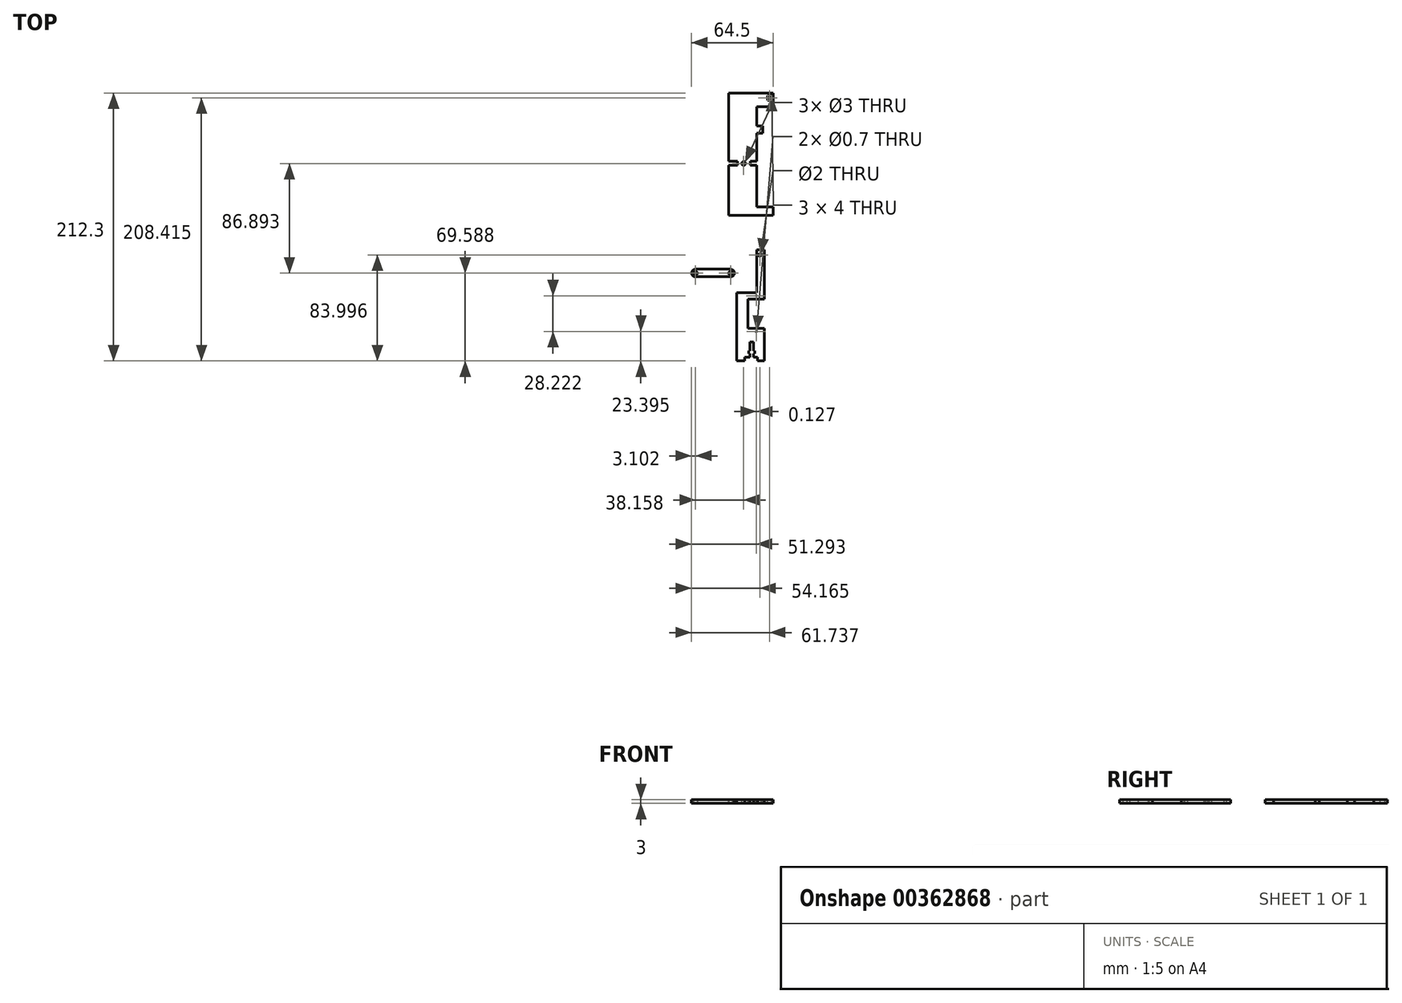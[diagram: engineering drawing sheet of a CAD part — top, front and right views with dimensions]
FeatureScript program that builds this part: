
annotation { "Feature Type Name" : "Feature", "Feature Type Description" : "" }
export const myFeature = defineFeature(function(context is Context, id is Id, definition is map)
    precondition{}
    {
        {
            var Q0;
            Q0=qCreatedBy(makeId("Top.planeOp"),FACE);
            var sketch = newSketch(context, id + "F0", { "sketchPlane" : qUnion([Q0])});
            skLineSegment(sketch, "E0.bottom", {"start": v(-45.73, -4.7) * mm, "end": v(-11.73, -4.7) * mm});
            skLineSegment(sketch, "E0.top", {"start": v(-45.73, 1.3) * mm, "end": v(-11.73, 1.3) * mm});
            skLineSegment(sketch, "E0.left", {"start": v(-45.73, -4.7) * mm, "end": v(-45.73, 1.3) * mm});
            skLineSegment(sketch, "E0.right", {"start": v(-11.73, -4.7) * mm, "end": v(-11.73, 1.3) * mm});
            skSolve(sketch);
        }
        {
            var Q0;
            Q0 = qSketchRegion(id + "F0", true);
            extrude(context, id + "F1", {"entities" : qUnion([Q0]), "depth" : 3 * mm});
        }
        {
            var Q0;
            Q0=makeQuery(id+"F1.opExtrude","SWEPT_EDGE",EDGE,{"disambiguationData":[OSD([sQuery(id+"F0.wireOp",EDGE,"E0.bottom"),sQuery(id+"F0.wireOp",EDGE,"E0.right")])]});
            var Q1;
            Q1=makeQuery(id+"F1.opExtrude","SWEPT_EDGE",EDGE,{"disambiguationData":[OSD([sQuery(id+"F0.wireOp",EDGE,"E0.top"),sQuery(id+"F0.wireOp",EDGE,"E0.right")])]});
            fillet(context, id + "F2", {"entities" : qUnion([Q0, Q1]), "radius" : 3.1 * mm, "tangentPropagation" : true, "allowEdgeOverflow" : false});
        }
        {
            var Q0;
            Q0=makeQuery(id+"F1.opExtrude","SWEPT_EDGE",EDGE,{"disambiguationData":[OSD([sQuery(id+"F0.wireOp",EDGE,"E0.bottom"),sQuery(id+"F0.wireOp",EDGE,"E0.left")])]});
            var Q1;
            Q1=makeQuery(id+"F1.opExtrude","SWEPT_EDGE",EDGE,{"disambiguationData":[OSD([sQuery(id+"F0.wireOp",EDGE,"E0.top"),sQuery(id+"F0.wireOp",EDGE,"E0.left")])]});
            fillet(context, id + "F3", {"entities" : qUnion([Q0, Q1]), "radius" : 3.1 * mm, "tangentPropagation" : true, "allowEdgeOverflow" : false});
        }
        {
            var Q0;
            Q0=makeQuery(id+"F1.opExtrude","CAP_FACE",FACE,{"disambiguationData":[OSD([sQuery(id+"F0.wireOp",EDGE,"E0.bottom"),sQuery(id+"F0.wireOp",EDGE,"E0.top"),sQuery(id+"F0.wireOp",EDGE,"E0.left"),sQuery(id+"F0.wireOp",EDGE,"E0.right")])],"isStart":true});
            var sketch = newSketch(context, id + "F4", { "sketchPlane" : qUnion([Q0])});
            skCircle(sketch, "E1", {"center": v(-42.63, 1.8) * mm, "radius": 1.5 * mm});
            skCircle(sketch, "E2", {"center": v(-14.83, 1.8) * mm, "radius": 1.5 * mm});
            skSolve(sketch);
        }
        {
            var Q0;
            Q0 = qSketchRegion(id + "F4", true);
            extrude(context, id + "F5", {"entities" : qUnion([Q0]), "operationType" : NewBodyOperationType.REMOVE, "oppositeDirection" : true, "depth" : 25.8 * mm});
        }
        {
            var Q0;
            Q0=qCreatedBy(makeId("Top.planeOp"),FACE);
            var sketch = newSketch(context, id + "F6", { "sketchPlane" : qUnion([Q0])});
            skLineSegment(sketch, "E3.bottom", {"start": v(-16.23, 140.91) * mm, "end": v(18.77, 140.91) * mm});
            skLineSegment(sketch, "E3.top", {"start": v(-16.23, 43.91) * mm, "end": v(18.77, 43.91) * mm});
            skLineSegment(sketch, "E3.left", {"start": v(-16.23, 140.91) * mm, "end": v(-16.23, 43.91) * mm});
            skLineSegment(sketch, "E3.right", {"start": v(18.77, 140.91) * mm, "end": v(18.77, 43.91) * mm});
            skSolve(sketch);
        }
        {
            var Q0;
            Q0=makeQuery(id+"F6.imprint","IMPRINT",FACE,{"disambiguationData":[TD([[makeQuery(id+"F6.imprint","IMPRINT",EDGE,{"derivedFrom":sQuery(id+"F6.wireOp",EDGE,"E3.bottom")}),-1.0]])]});
            extrude(context, id + "F7", {"entities" : qUnion([Q0]), "depth" : 3 * mm});
        }
        {
            var Q0;
            Q0=makeQuery(id+"F7.opExtrude","CAP_FACE",FACE,{"disambiguationData":[OSD([sQuery(id+"F6.wireOp",EDGE,"E3.bottom"),sQuery(id+"F6.wireOp",EDGE,"E3.top"),sQuery(id+"F6.wireOp",EDGE,"E3.left"),sQuery(id+"F6.wireOp",EDGE,"E3.right")])],"isStart":false});
            var sketch = newSketch(context, id + "F8", { "sketchPlane" : qUnion([Q0])});
            skLineSegment(sketch, "E4.bottom", {"start": v(18.77, 140.91) * mm, "end": v(14.43, 140.91) * mm});
            skLineSegment(sketch, "E4.top", {"start": v(18.77, 129.91) * mm, "end": v(14.43, 129.91) * mm});
            skLineSegment(sketch, "E4.left", {"start": v(18.77, 140.91) * mm, "end": v(18.77, 129.91) * mm});
            skLineSegment(sketch, "E4.right", {"start": v(14.43, 140.91) * mm, "end": v(14.43, 129.91) * mm});
            skLineSegment(sketch, "E5.bottom", {"start": v(18.77, 129.91) * mm, "end": v(5.77, 129.91) * mm});
            skLineSegment(sketch, "E5.top", {"start": v(18.77, 114.91) * mm, "end": v(5.77, 114.91) * mm});
            skLineSegment(sketch, "E5.left", {"start": v(18.77, 129.91) * mm, "end": v(18.77, 114.91) * mm});
            skLineSegment(sketch, "E5.right", {"start": v(5.77, 129.91) * mm, "end": v(5.77, 114.91) * mm});
            skSolve(sketch);
        }
        {
            var Q0;
            Q0=makeQuery(id+"F8.imprint","IMPRINT",FACE,{"disambiguationData":[TD([[makeQuery(id+"F8.imprint","IMPRINT",EDGE,{"derivedFrom":sQuery(id+"F8.wireOp",EDGE,"E5.top")}),-1.0]])]});
            extrude(context, id + "F9", {"entities" : qUnion([Q0]), "operationType" : NewBodyOperationType.REMOVE, "oppositeDirection" : true, "depth" : 65 * mm});
        }
        {
            var Q0;
            Q0=makeQuery(id+"F7.opExtrude","CAP_FACE",FACE,{"disambiguationData":[OSD([sQuery(id+"F6.wireOp",EDGE,"E3.bottom"),sQuery(id+"F6.wireOp",EDGE,"E3.top"),sQuery(id+"F6.wireOp",EDGE,"E3.left"),sQuery(id+"F6.wireOp",EDGE,"E3.right")])],"isStart":false});
            var sketch = newSketch(context, id + "F10", { "sketchPlane" : qUnion([Q0])});
            skLineSegment(sketch, "E6.bottom", {"start": v(18.77, 50.59) * mm, "end": v(5.77, 50.59) * mm});
            skLineSegment(sketch, "E6.top", {"start": v(18.77, 109.24) * mm, "end": v(5.77, 109.24) * mm});
            skLineSegment(sketch, "E6.left", {"start": v(18.77, 50.59) * mm, "end": v(18.77, 109.24) * mm});
            skLineSegment(sketch, "E6.right", {"start": v(5.77, 50.59) * mm, "end": v(5.77, 109.24) * mm});
            skSolve(sketch);
        }
        {
            var Q0;
            Q0=makeQuery(id+"F10.imprint","IMPRINT",FACE,{"disambiguationData":[TD([[makeQuery(id+"F10.imprint","IMPRINT",EDGE,{"derivedFrom":sQuery(id+"F10.wireOp",EDGE,"E6.bottom")}),-1.0]])]});
            extrude(context, id + "F11", {"entities" : qUnion([Q0]), "operationType" : NewBodyOperationType.REMOVE, "oppositeDirection" : true, "depth" : 25 * mm});
        }
        {
            var Q0;
            Q0=makeQuery(id+"F7.opExtrude","CAP_FACE",FACE,{"disambiguationData":[OSD([sQuery(id+"F6.wireOp",EDGE,"E3.bottom"),sQuery(id+"F6.wireOp",EDGE,"E3.top"),sQuery(id+"F6.wireOp",EDGE,"E3.left"),sQuery(id+"F6.wireOp",EDGE,"E3.right")])],"isStart":false});
            var sketch = newSketch(context, id + "F12", { "sketchPlane" : qUnion([Q0])});
            skLineSegment(sketch, "E7", {"start": v(5.77, 50.59) * mm, "end": v(5.77, 83.59) * mm});
            skLineSegment(sketch, "E8.bottom", {"start": v(5.77, 83.59) * mm, "end": v(0.77, 83.59) * mm});
            skLineSegment(sketch, "E8.top", {"start": v(5.77, 86.83) * mm, "end": v(0.77, 86.83) * mm});
            skLineSegment(sketch, "E8.left", {"start": v(5.77, 83.59) * mm, "end": v(5.77, 86.83) * mm});
            skLineSegment(sketch, "E8.right", {"start": v(0.77, 83.59) * mm, "end": v(0.77, 86.83) * mm});
            skLineSegment(sketch, "E9.bottom", {"start": v(0.77, 83.59) * mm, "end": v(-9.23, 83.59) * mm});
            skLineSegment(sketch, "E9.top", {"start": v(0.77, 86.83) * mm, "end": v(-9.23, 86.83) * mm});
            skLineSegment(sketch, "E9.right", {"start": v(-9.23, 83.59) * mm, "end": v(-9.23, 86.83) * mm});
            skLineSegment(sketch, "E10.bottom", {"start": v(-9.23, 83.59) * mm, "end": v(-16.23, 83.59) * mm});
            skLineSegment(sketch, "E10.top", {"start": v(-9.23, 86.79) * mm, "end": v(-16.23, 86.79) * mm});
            skLineSegment(sketch, "E10.left", {"start": v(-9.23, 83.59) * mm, "end": v(-9.23, 86.79) * mm});
            skLineSegment(sketch, "E10.right", {"start": v(-16.23, 83.59) * mm, "end": v(-16.23, 86.79) * mm});
            skSolve(sketch);
        }
        {
            var Q0;
            {var subQ0=sQuery(id+"F12.wireOp",EDGE,"E8.bottom");Q0=makeQuery(id+"F12.imprint","IMPRINT",FACE,{"disambiguationData":[TD([[makeQuery(id+"F12.imprint","IMPRINT",EDGE,{"derivedFrom":subQ0}),-1.0]])]});}
            var Q1;
            Q1=makeQuery(id+"F12.imprint","IMPRINT",FACE,{"disambiguationData":[TD([[makeQuery(id+"F12.imprint","IMPRINT",EDGE,{"derivedFrom":sQuery(id+"F12.wireOp",EDGE,"E10.bottom")}),-1.0]])]});
            extrude(context, id + "F13", {"entities" : qUnion([Q0, Q1]), "operationType" : NewBodyOperationType.REMOVE, "oppositeDirection" : true, "depth" : 35.3 * mm});
        }
        {
            var Q0;
            Q0=makeQuery(id+"F7.opExtrude","CAP_FACE",FACE,{"disambiguationData":[OSD([sQuery(id+"F6.wireOp",EDGE,"E3.bottom"),sQuery(id+"F6.wireOp",EDGE,"E3.top"),sQuery(id+"F6.wireOp",EDGE,"E3.left"),sQuery(id+"F6.wireOp",EDGE,"E3.right")])],"isStart":false});
            var sketch = newSketch(context, id + "F14", { "sketchPlane" : qUnion([Q0])});
            skCircle(sketch, "E11", {"center": v(-4.47, 85.1) * mm, "radius": 1.5 * mm});
            skSolve(sketch);
        }
        {
            var Q0;
            Q0=makeQuery(id+"F14.imprint","IMPRINT",FACE,{"disambiguationData":[TD([[makeQuery(id+"F14.imprint","IMPRINT",EDGE,{"derivedFrom":sQuery(id+"F14.wireOp",EDGE,"E11")}),1.0]])]});
            extrude(context, id + "F15", {"entities" : qUnion([Q0]), "operationType" : NewBodyOperationType.REMOVE, "oppositeDirection" : true, "depth" : 25 * mm});
        }
        {
            var Q0;
            Q0=makeQuery(id+"F7.opExtrude","CAP_FACE",FACE,{"disambiguationData":[OSD([sQuery(id+"F6.wireOp",EDGE,"E3.bottom"),sQuery(id+"F6.wireOp",EDGE,"E3.top"),sQuery(id+"F6.wireOp",EDGE,"E3.left"),sQuery(id+"F6.wireOp",EDGE,"E3.right")])],"isStart":false});
            var sketch = newSketch(context, id + "F16", { "sketchPlane" : qUnion([Q0])});
            skLineSegment(sketch, "E12.bottom", {"start": v(18.77, 109.24) * mm, "end": v(10.54, 109.24) * mm});
            skLineSegment(sketch, "E12.top", {"start": v(18.77, 114.91) * mm, "end": v(10.54, 114.91) * mm});
            skLineSegment(sketch, "E12.left", {"start": v(18.77, 109.24) * mm, "end": v(18.77, 114.91) * mm});
            skLineSegment(sketch, "E12.right", {"start": v(10.54, 109.24) * mm, "end": v(10.54, 114.91) * mm});
            skLineSegment(sketch, "E13.bottom", {"start": v(14.5, 135.03) * mm, "end": v(17.5, 135.03) * mm});
            skLineSegment(sketch, "E13.top", {"start": v(14.5, 139.03) * mm, "end": v(17.5, 139.03) * mm});
            skLineSegment(sketch, "E13.left", {"start": v(14.5, 135.03) * mm, "end": v(14.5, 139.03) * mm});
            skLineSegment(sketch, "E13.right", {"start": v(17.5, 135.03) * mm, "end": v(17.5, 139.03) * mm});
            skSolve(sketch);
        }
        {
            var Q0;
            Q0 = qSketchRegion(id + "F16", true);
            extrude(context, id + "F17", {"entities" : qUnion([Q0]), "operationType" : NewBodyOperationType.REMOVE, "oppositeDirection" : true, "depth" : 25 * mm});
        }
        {
            var Q0;
            Q0=qCreatedBy(makeId("Top.planeOp"),FACE);
            var sketch = newSketch(context, id + "F18", { "sketchPlane" : qUnion([Q0])});
            skLineSegment(sketch, "E14.bottom", {"start": v(-10.09, -71.4) * mm, "end": v(11.91, -71.4) * mm});
            skLineSegment(sketch, "E14.top", {"start": v(-10.09, 16.6) * mm, "end": v(11.91, 16.6) * mm});
            skLineSegment(sketch, "E14.left", {"start": v(-10.09, -71.4) * mm, "end": v(-10.09, 16.6) * mm});
            skLineSegment(sketch, "E14.right", {"start": v(11.91, -71.4) * mm, "end": v(11.91, 16.6) * mm});
            skSolve(sketch);
        }
        {
            var Q0;
            Q0 = qSketchRegion(id + "F18", true);
            extrude(context, id + "F19", {"entities" : qUnion([Q0]), "depth" : 3 * mm});
        }
        {
            var Q0;
            Q0=makeQuery(id+"F19.opExtrude","CAP_FACE",FACE,{"disambiguationData":[OSD([sQuery(id+"F18.wireOp",EDGE,"E14.bottom"),sQuery(id+"F18.wireOp",EDGE,"E14.top"),sQuery(id+"F18.wireOp",EDGE,"E14.left"),sQuery(id+"F18.wireOp",EDGE,"E14.right")])],"isStart":false});
            var sketch = newSketch(context, id + "F20", { "sketchPlane" : qUnion([Q0])});
            skLineSegment(sketch, "E15.bottom", {"start": v(-10.09, 16.6) * mm, "end": v(5.91, 16.6) * mm});
            skLineSegment(sketch, "E15.top", {"start": v(-10.09, -17.4) * mm, "end": v(5.91, -17.4) * mm});
            skLineSegment(sketch, "E15.left", {"start": v(-10.09, 16.6) * mm, "end": v(-10.09, -17.4) * mm});
            skLineSegment(sketch, "E15.right", {"start": v(5.91, 16.6) * mm, "end": v(5.91, -17.4) * mm});
            skSolve(sketch);
        }
        {
            var Q0;
            Q0 = qSketchRegion(id + "F20", true);
            extrude(context, id + "F21", {"entities" : qUnion([Q0]), "operationType" : NewBodyOperationType.REMOVE, "oppositeDirection" : true, "depth" : 14.5 * mm});
        }
        {
            var Q0;
            Q0=makeQuery(id+"F19.opExtrude","CAP_FACE",FACE,{"disambiguationData":[OSD([sQuery(id+"F18.wireOp",EDGE,"E14.bottom"),sQuery(id+"F18.wireOp",EDGE,"E14.top"),sQuery(id+"F18.wireOp",EDGE,"E14.left"),sQuery(id+"F18.wireOp",EDGE,"E14.right")])],"isStart":false});
            var sketch = newSketch(context, id + "F22", { "sketchPlane" : qUnion([Q0])});
            skLineSegment(sketch, "E16", {"start": v(11.91, 16.6) * mm, "end": v(11.91, -22.4) * mm});
            skLineSegment(sketch, "E17.bottom", {"start": v(11.91, -22.4) * mm, "end": v(-1.09, -22.4) * mm});
            skLineSegment(sketch, "E17.top", {"start": v(11.91, -45.4) * mm, "end": v(-1.09, -45.4) * mm});
            skLineSegment(sketch, "E17.left", {"start": v(11.91, -22.4) * mm, "end": v(11.91, -45.4) * mm});
            skLineSegment(sketch, "E17.right", {"start": v(-1.09, -22.4) * mm, "end": v(-1.09, -45.4) * mm});
            skSolve(sketch);
        }
        {
            var Q0;
            Q0 = qSketchRegion(id + "F22", true);
            extrude(context, id + "F23", {"entities" : qUnion([Q0]), "operationType" : NewBodyOperationType.REMOVE, "oppositeDirection" : true, "depth" : 25 * mm});
        }
        {
            var Q0;
            Q0=makeQuery(id+"F19.opExtrude","CAP_FACE",FACE,{"disambiguationData":[OSD([sQuery(id+"F18.wireOp",EDGE,"E14.bottom"),sQuery(id+"F18.wireOp",EDGE,"E14.top"),sQuery(id+"F18.wireOp",EDGE,"E14.left"),sQuery(id+"F18.wireOp",EDGE,"E14.right")])],"isStart":false});
            var sketch = newSketch(context, id + "F24", { "sketchPlane" : qUnion([Q0])});
            skLineSegment(sketch, "E18", {"start": v(11.91, -71.4) * mm, "end": v(6.41, -71.4) * mm});
            skLineSegment(sketch, "E19.bottom", {"start": v(6.41, -71.4) * mm, "end": v(-3.59, -71.4) * mm});
            skLineSegment(sketch, "E19.top", {"start": v(6.41, -68.4) * mm, "end": v(-3.59, -68.4) * mm});
            skLineSegment(sketch, "E19.left", {"start": v(6.41, -71.4) * mm, "end": v(6.41, -68.4) * mm});
            skLineSegment(sketch, "E19.right", {"start": v(-3.59, -71.4) * mm, "end": v(-3.59, -68.4) * mm});
            skSolve(sketch);
        }
        {
            var Q0;
            Q0 = qSketchRegion(id + "F24", true);
            extrude(context, id + "F25", {"entities" : qUnion([Q0]), "operationType" : NewBodyOperationType.REMOVE, "oppositeDirection" : true, "depth" : 25 * mm});
        }
        {
            var Q0;
            Q0=makeQuery(id+"F19.opExtrude","CAP_FACE",FACE,{"disambiguationData":[OSD([sQuery(id+"F18.wireOp",EDGE,"E14.bottom"),sQuery(id+"F18.wireOp",EDGE,"E14.top"),sQuery(id+"F18.wireOp",EDGE,"E14.left"),sQuery(id+"F18.wireOp",EDGE,"E14.right")])],"isStart":false});
            var sketch = newSketch(context, id + "F26", { "sketchPlane" : qUnion([Q0])});
            skLineSegment(sketch, "E20", {"start": v(6.41, -68.4) * mm, "end": v(3.41, -68.4) * mm});
            skLineSegment(sketch, "E21.bottom", {"start": v(3.41, -68.4) * mm, "end": v(0.41, -68.4) * mm});
            skLineSegment(sketch, "E21.top", {"start": v(3.41, -56.4) * mm, "end": v(0.41, -56.4) * mm});
            skLineSegment(sketch, "E21.left", {"start": v(3.41, -68.4) * mm, "end": v(3.41, -56.4) * mm});
            skLineSegment(sketch, "E21.right", {"start": v(0.41, -68.4) * mm, "end": v(0.41, -56.4) * mm});
            skSolve(sketch);
        }
        {
            var Q0;
            Q0 = qSketchRegion(id + "F26", true);
            extrude(context, id + "F27", {"entities" : qUnion([Q0]), "operationType" : NewBodyOperationType.REMOVE, "oppositeDirection" : true, "depth" : 25 * mm});
        }
        {
            var Q0;
            Q0=makeQuery(id+"F19.opExtrude","CAP_FACE",FACE,{"disambiguationData":[OSD([sQuery(id+"F18.wireOp",EDGE,"E14.bottom"),sQuery(id+"F18.wireOp",EDGE,"E14.top"),sQuery(id+"F18.wireOp",EDGE,"E14.left"),sQuery(id+"F18.wireOp",EDGE,"E14.right")])],"isStart":false});
            var sketch = newSketch(context, id + "F28", { "sketchPlane" : qUnion([Q0])});
            skLineSegment(sketch, "E22", {"start": v(0.41, -68.4) * mm, "end": v(0.41, -65.4) * mm});
            skLineSegment(sketch, "E23.bottom", {"start": v(-0.49, -65.44) * mm, "end": v(4.42, -65.44) * mm});
            skLineSegment(sketch, "E23.top", {"start": v(-0.49, -63.44) * mm, "end": v(4.42, -63.44) * mm});
            skLineSegment(sketch, "E23.left", {"start": v(-0.49, -65.44) * mm, "end": v(-0.49, -63.44) * mm});
            skLineSegment(sketch, "E23.right", {"start": v(4.42, -65.44) * mm, "end": v(4.42, -63.44) * mm});
            skSolve(sketch);
        }
        {
            var Q0;
            Q0 = qSketchRegion(id + "F28", true);
            extrude(context, id + "F29", {"entities" : qUnion([Q0]), "operationType" : NewBodyOperationType.REMOVE, "oppositeDirection" : true, "depth" : 25 * mm});
        }
        {
            var Q0;
            Q0=makeQuery(id+"F19.opExtrude","CAP_FACE",FACE,{"disambiguationData":[OSD([sQuery(id+"F18.wireOp",EDGE,"E14.bottom"),sQuery(id+"F18.wireOp",EDGE,"E14.top"),sQuery(id+"F18.wireOp",EDGE,"E14.left"),sQuery(id+"F18.wireOp",EDGE,"E14.right")])],"isStart":false});
            var sketch = newSketch(context, id + "F30", { "sketchPlane" : qUnion([Q0])});
            skCircle(sketch, "E24", {"center": v(8.44, 12.6) * mm, "radius": 1 * mm});
            skCircle(sketch, "E25", {"center": v(5.56, -19.77) * mm, "radius": 0.35 * mm});
            skCircle(sketch, "E26", {"center": v(5.69, -48) * mm, "radius": 0.35 * mm});
            skSolve(sketch);
        }
        {
            var Q0;
            Q0 = qSketchRegion(id + "F30", true);
            extrude(context, id + "F31", {"entities" : qUnion([Q0]), "operationType" : NewBodyOperationType.REMOVE, "oppositeDirection" : true, "depth" : 25 * mm});
        }
    });
